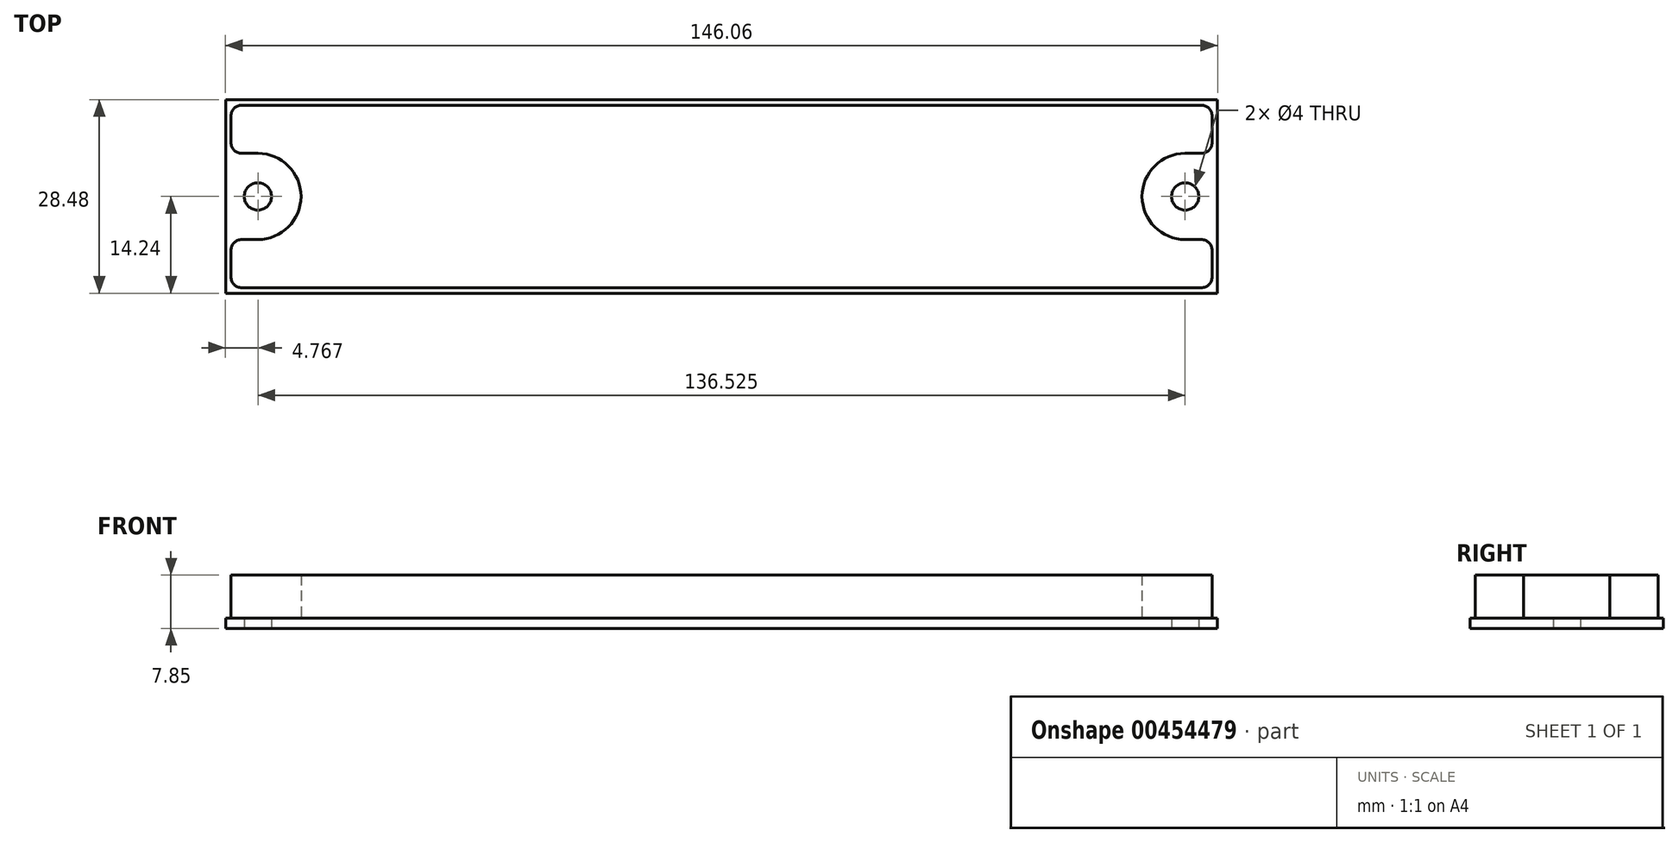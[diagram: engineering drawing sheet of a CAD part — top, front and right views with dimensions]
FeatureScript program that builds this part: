
annotation { "Feature Type Name" : "Feature", "Feature Type Description" : "" }
export const myFeature = defineFeature(function(context is Context, id is Id, definition is map)
    precondition{}
    {
        {
            var Q0;
            Q0=qCreatedBy(makeId("Top.planeOp"),FACE);
            var sketch = newSketch(context, id + "F0", { "sketchPlane" : qUnion([Q0])});
            skLineSegment(sketch, "E0.bottom", {"start": v(-73.03, 14.24) * mm, "end": v(73.03, 14.24) * mm, "construction": true});
            skLineSegment(sketch, "E0.top", {"start": v(-73.03, -14.24) * mm, "end": v(73.03, -14.24) * mm, "construction": true});
            skLineSegment(sketch, "E0.left", {"start": v(-73.03, 14.24) * mm, "end": v(-73.03, -14.24) * mm, "construction": true});
            skLineSegment(sketch, "E0.right", {"start": v(73.03, 14.24) * mm, "end": v(73.03, -14.24) * mm, "construction": true});
            skCircle(sketch, "E1", {"center": v(-68.26, 0) * mm, "radius": 4.76 * mm});
            skPoint(sketch, "E2.third.point.positionSnap0", {"position": v(73.03, 0) * mm});
            skCircle(sketch, "E3", {"center": v(68.26, 0) * mm, "radius": 4.76 * mm});
            skPoint(sketch, "E4", {"position": v(0, 14.24) * mm});
            skLineSegment(sketch, "E5.bottom", {"start": v(-73.03, 14.24) * mm, "end": v(73.03, 14.24) * mm});
            skLineSegment(sketch, "E5.top", {"start": v(-73.03, -14.24) * mm, "end": v(73.03, -14.24) * mm});
            skLineSegment(sketch, "E5.left", {"start": v(-73.03, 14.24) * mm, "end": v(-73.03, -14.24) * mm});
            skLineSegment(sketch, "E5.right", {"start": v(73.03, 14.24) * mm, "end": v(73.03, -14.24) * mm});
            skCircle(sketch, "E6", {"center": v(-68.26, 0) * mm, "radius": 2 * mm});
            skCircle(sketch, "E7", {"center": v(68.26, 0) * mm, "radius": 2 * mm});
            skArc(sketch, "E8", {"start": v(68.26, 6.35) * mm, "mid": v(61.91, 0) * mm, "end": v(68.26, -6.35) * mm});
            skArc(sketch, "E9", {"start": v(-68.26, -6.35) * mm, "mid": v(-61.91, 0) * mm, "end": v(-68.26, 6.35) * mm});
            skLineSegment(sketch, "E10", {"start": v(68.26, 6.35) * mm, "end": v(73.03, 6.35) * mm});
            skLineSegment(sketch, "E11", {"start": v(68.26, -6.35) * mm, "end": v(73.03, -6.35) * mm});
            skLineSegment(sketch, "E12", {"start": v(-68.26, 6.35) * mm, "end": v(-73.03, 6.35) * mm});
            skLineSegment(sketch, "E13", {"start": v(-68.26, -6.35) * mm, "end": v(-73.03, -6.35) * mm});
            skSolve(sketch);
        }
        {
            var Q0;
            {var subQ3=sQuery(id+"F0.wireOp",EDGE,"E5.bottom");Q0=makeQuery(id+"F0.imprint","IMPRINT",FACE,{"disambiguationData":[TD([[makeQuery(id+"F0.imprint","IMPRINT",EDGE,{"derivedFrom":subQ3}),-1.0]])]});}
            var Q1;
            {var subQ2=sQuery(id+"F0.wireOp",EDGE,"E1");Q1=makeQuery(id+"F0.imprint","IMPRINT",FACE,{"disambiguationData":[TD([[makeQuery(id+"F0.imprint","IMPRINT",EDGE,{"derivedFrom":subQ2}),-1.0]])]});}
            var Q2;
            Q2=makeQuery(id+"F0.imprint","IMPRINT",FACE,{"disambiguationData":[TD([[makeQuery(id+"F0.imprint","IMPRINT",EDGE,{"derivedFrom":sQuery(id+"F0.wireOp",EDGE,"E1")}),1.0]])]});
            var Q3;
            {var subQ2=sQuery(id+"F0.wireOp",EDGE,"E1");Q3=makeQuery(id+"F0.imprint","IMPRINT",FACE,{"disambiguationData":[TD([[makeQuery(id+"F0.imprint","IMPRINT",EDGE,{"derivedFrom":subQ2}),-1.0]])]});}
            var Q4;
            Q4=makeQuery(id+"F0.imprint","IMPRINT",FACE,{"disambiguationData":[TD([[makeQuery(id+"F0.imprint","IMPRINT",EDGE,{"derivedFrom":sQuery(id+"F0.wireOp",EDGE,"E1")}),1.0]])]});
            var Q5;
            {var subQ2=sQuery(id+"F0.wireOp",EDGE,"E3");Q5=makeQuery(id+"F0.imprint","IMPRINT",FACE,{"disambiguationData":[TD([[makeQuery(id+"F0.imprint","IMPRINT",EDGE,{"derivedFrom":subQ2}),-1.0]])]});}
            var Q6;
            Q6=makeQuery(id+"F0.imprint","IMPRINT",FACE,{"disambiguationData":[TD([[makeQuery(id+"F0.imprint","IMPRINT",EDGE,{"derivedFrom":sQuery(id+"F0.wireOp",EDGE,"E3")}),1.0]])]});
            var Q7;
            {var subQ0=sQuery(id+"F0.wireOp",EDGE,"E3");Q7=makeQuery(id+"F0.imprint","IMPRINT",FACE,{"disambiguationData":[TD([[makeQuery(id+"F0.imprint","IMPRINT",EDGE,{"derivedFrom":subQ0}),-1.0]])]});}
            var Q8;
            Q8=makeQuery(id+"F0.imprint","IMPRINT",FACE,{"disambiguationData":[TD([[makeQuery(id+"F0.imprint","IMPRINT",EDGE,{"derivedFrom":sQuery(id+"F0.wireOp",EDGE,"E3")}),1.0]])]});
            extrude(context, id + "F1", {"entities" : qUnion([Q0, Q1, Q2, Q3, Q4, Q5, Q6, Q7, Q8]), "depth" : 1.5 * mm});
        }
        {
            var Q0;
            Q0=makeQuery(id+"F1.opExtrude","CAP_FACE",FACE,{"disambiguationData":[OSD([sQuery(id+"F0.wireOp",EDGE,"E5.bottom"),sQuery(id+"F0.wireOp",EDGE,"E5.top"),sQuery(id+"F0.wireOp",EDGE,"E5.left"),sQuery(id+"F0.wireOp",EDGE,"E5.right"),sQuery(id+"F0.wireOp",EDGE,"E6"),sQuery(id+"F0.wireOp",EDGE,"E7"),sQuery(id+"F0.wireOp",EDGE,"E6"),sQuery(id+"F0.wireOp",EDGE,"E7")])],"isStart":false});
            var sketch = newSketch(context, id + "F2", { "sketchPlane" : qUnion([Q0])});
            skLineSegment(sketch, "E14.0", {"start": v(68.26, -6.35) * mm, "end": v(70.64, -6.35) * mm});
            skArc(sketch, "E14.1", {"start": v(68.26, 6.35) * mm, "mid": v(61.91, 0) * mm, "end": v(68.26, -6.35) * mm});
            skLineSegment(sketch, "E14.2", {"start": v(68.26, 6.35) * mm, "end": v(70.64, 6.35) * mm});
            skLineSegment(sketch, "E15.0", {"start": v(73.03, 14.24) * mm, "end": v(73.03, -14.24) * mm});
            skLineSegment(sketch, "E15.4", {"start": v(-73.03, -14.24) * mm, "end": v(73.03, -14.24) * mm});
            skLineSegment(sketch, "E15.5", {"start": v(-73.03, 14.24) * mm, "end": v(-73.03, -14.24) * mm});
            skLineSegment(sketch, "E15.6", {"start": v(-68.26, -6.35) * mm, "end": v(-70.64, -6.35) * mm});
            skArc(sketch, "E15.7", {"start": v(-68.26, -6.35) * mm, "mid": v(-61.91, 0) * mm, "end": v(-68.26, 6.35) * mm});
            skLineSegment(sketch, "E15.8", {"start": v(-68.26, 6.35) * mm, "end": v(-70.64, 6.35) * mm});
            skLineSegment(sketch, "E15.9", {"start": v(-73.03, 14.24) * mm, "end": v(73.03, 14.24) * mm});
            skArc(sketch, "E15.10", {"start": v(-68.26, -6.35) * mm, "mid": v(-61.91, 0) * mm, "end": v(-68.26, 6.35) * mm});
            skLineSegment(sketch, "E15.11", {"start": v(-68.26, -6.35) * mm, "end": v(-70.64, -6.35) * mm});
            skLineSegment(sketch, "E15.12", {"start": v(-68.26, 6.35) * mm, "end": v(-70.64, 6.35) * mm});
            skLineSegment(sketch, "E16.0", {"start": v(-70.64, 13.44) * mm, "end": v(70.64, 13.44) * mm});
            skLineSegment(sketch, "E16.1", {"start": v(-72.23, 11.85) * mm, "end": v(-72.23, 7.94) * mm});
            skLineSegment(sketch, "E16.2", {"start": v(-70.64, -13.44) * mm, "end": v(70.64, -13.44) * mm});
            skLineSegment(sketch, "E16.3", {"start": v(72.23, 11.85) * mm, "end": v(72.23, 7.94) * mm});
            skPoint(sketch, "E17", {"position": v(-72.23, -6.35) * mm});
            skPoint(sketch, "E18", {"position": v(-72.23, 6.35) * mm});
            skPoint(sketch, "E19", {"position": v(72.23, -6.35) * mm});
            skPoint(sketch, "E20", {"position": v(72.23, 6.35) * mm});
            skLineSegment(sketch, "E21.trimOffspring", {"start": v(72.23, 7.94) * mm, "end": v(72.23, -7.94) * mm});
            skPoint(sketch, "E22.orphan", {"position": v(73.03, 6.35) * mm});
            skPoint(sketch, "E23.orphan", {"position": v(73.03, -6.35) * mm});
            skLineSegment(sketch, "E24.trimOffspring", {"start": v(72.23, -7.94) * mm, "end": v(72.23, -11.85) * mm});
            skLineSegment(sketch, "E25.trimOffspring", {"start": v(-72.23, -7.94) * mm, "end": v(-72.23, -11.85) * mm});
            skPoint(sketch, "E26.orphan", {"position": v(-73.03, -6.35) * mm});
            skPoint(sketch, "E27.orphan", {"position": v(-73.03, 6.35) * mm});
            skLineSegment(sketch, "E28.trimOffspring", {"start": v(-72.23, 7.94) * mm, "end": v(-72.23, -7.94) * mm});
            skArc(sketch, "E29.filletArc", {"start": v(-72.23, 7.94) * mm, "mid": v(-71.76, 6.82) * mm, "end": v(-70.64, 6.35) * mm});
            skArc(sketch, "E30.filletArc", {"start": v(-70.64, -6.35) * mm, "mid": v(-71.76, -6.82) * mm, "end": v(-72.23, -7.94) * mm});
            skPoint(sketch, "E31.visualSharp", {"position": v(-72.23, 13.44) * mm});
            skArc(sketch, "E31.filletArc", {"start": v(-70.64, 13.44) * mm, "mid": v(-71.76, 12.97) * mm, "end": v(-72.23, 11.85) * mm});
            skPoint(sketch, "E32.visualSharp", {"position": v(-72.23, -13.44) * mm});
            skArc(sketch, "E32.filletArc", {"start": v(-72.23, -11.85) * mm, "mid": v(-71.76, -12.97) * mm, "end": v(-70.64, -13.44) * mm});
            skPoint(sketch, "E33.visualSharp", {"position": v(72.23, -13.44) * mm});
            skArc(sketch, "E33.filletArc", {"start": v(70.64, -13.44) * mm, "mid": v(71.76, -12.97) * mm, "end": v(72.23, -11.85) * mm});
            skArc(sketch, "E34.filletArc", {"start": v(72.23, -7.94) * mm, "mid": v(71.76, -6.82) * mm, "end": v(70.64, -6.35) * mm});
            skArc(sketch, "E35.filletArc", {"start": v(70.64, 6.35) * mm, "mid": v(71.76, 6.82) * mm, "end": v(72.23, 7.94) * mm});
            skPoint(sketch, "E36.visualSharp", {"position": v(72.23, 13.44) * mm});
            skArc(sketch, "E36.filletArc", {"start": v(72.23, 11.85) * mm, "mid": v(71.76, 12.97) * mm, "end": v(70.64, 13.44) * mm});
            skSolve(sketch);
        }
        {
            var Q0;
            Q0=makeQuery(id+"F2.imprint","IMPRINT",FACE,{"disambiguationData":[TD([[makeQuery(id+"F2.imprint","IMPRINT",EDGE,{"derivedFrom":sQuery(id+"F2.wireOp",EDGE,"E14.0")}),-1.0]])]});
            var Q1;
            Q1=makeQuery(id+"F2.imprint","IMPRINT",FACE,{"disambiguationData":[TD([[makeQuery(id+"F2.imprint","IMPRINT",EDGE,{"derivedFrom":sQuery(id+"F2.wireOp",EDGE,"E14.2")}),1.0]])]});
            extrude(context, id + "F3", {"entities" : qUnion([Q0, Q1]), "depth" : 6.35 * mm});
        }
    });
